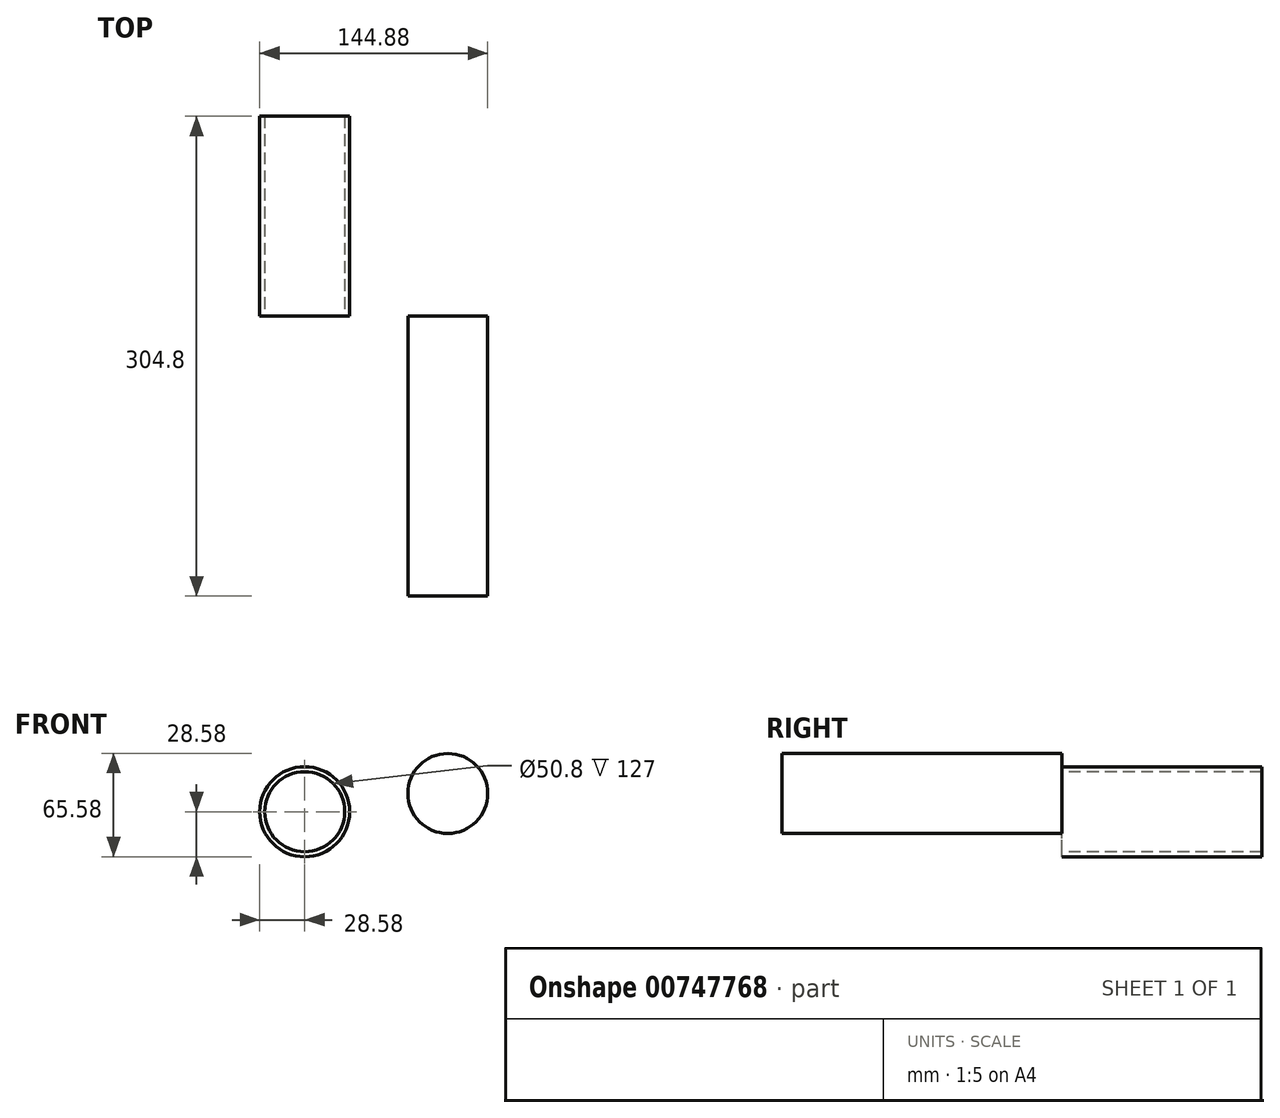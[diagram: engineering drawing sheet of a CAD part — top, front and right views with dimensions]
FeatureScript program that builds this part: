
annotation { "Feature Type Name" : "Feature", "Feature Type Description" : "" }
export const myFeature = defineFeature(function(context is Context, id is Id, definition is map)
    precondition{}
    {
        {
            var Q0;
            Q0=qCreatedBy(makeId("Front.planeOp"),FACE);
            var sketch = newSketch(context, id + "F0", { "sketchPlane" : qUnion([Q0])});
            skCircle(sketch, "E0", {"center": v(0, 0) * mm, "radius": 25.4 * mm});
            skCircle(sketch, "E1.0", {"center": v(0, 0) * mm, "radius": 28.58 * mm});
            skSolve(sketch);
        }
        {
            var Q0;
            Q0=makeQuery(id+"F0.imprint","IMPRINT",FACE,{"disambiguationData":[TD([[makeQuery(id+"F0.imprint","IMPRINT",EDGE,{"derivedFrom":sQuery(id+"F0.wireOp",EDGE,"E0")}),-1.0]])]});
            extrude(context, id + "F1", {"entities" : qUnion([Q0]), "oppositeDirection" : true, "depth" : 127 * mm, "offsetDistance" : 25.4 * mm});
        }
        {
            var Q0;
            Q0=qCreatedBy(makeId("Front.planeOp"),FACE);
            var sketch = newSketch(context, id + "F2", { "sketchPlane" : qUnion([Q0])});
            skCircle(sketch, "E2", {"center": v(90.9, 11.6) * mm, "radius": 25.4 * mm});
            skSolve(sketch);
        }
        {
            var Q0;
            Q0=makeQuery(id+"F2.imprint","IMPRINT",FACE,{"disambiguationData":[TD([[makeQuery(id+"F2.imprint","IMPRINT",EDGE,{"derivedFrom":sQuery(id+"F2.wireOp",EDGE,"E2")}),1.0]])]});
            extrude(context, id + "F3", {"entities" : qUnion([Q0]), "depth" : 177.8 * mm, "offsetDistance" : 25.4 * mm});
        }
    });
